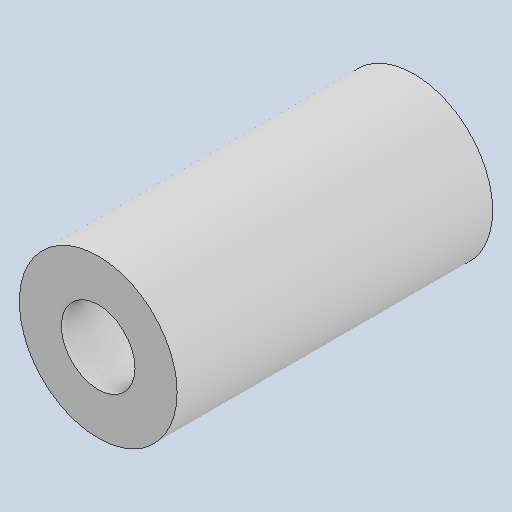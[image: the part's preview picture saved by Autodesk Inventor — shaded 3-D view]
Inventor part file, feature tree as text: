
AUTODESK INVENTOR PART (.ipt)
format: ipt  version: 2024 (Build 280153000, 153)  size: 96,768 bytes
history: native  units: in
note: dims shown in document units (in); Inventor stores cm internally (conversion verified against a paired STEP export)
features: other x3, sketch x1
ambient origin geometry x8: Origin, YZ Plane, XZ Plane, XY Plane, X Axis, Y Axis, Z Axis, Center Point
bodies: Solid1 (feature_tree)
feature tree (4):
  other  "Part5.ipt"
  other  "Solid1::Part5.ipt"
  other  "TaggingFeature1"
  sketch  "Sketch1"  dims[d0=0.3937in]
